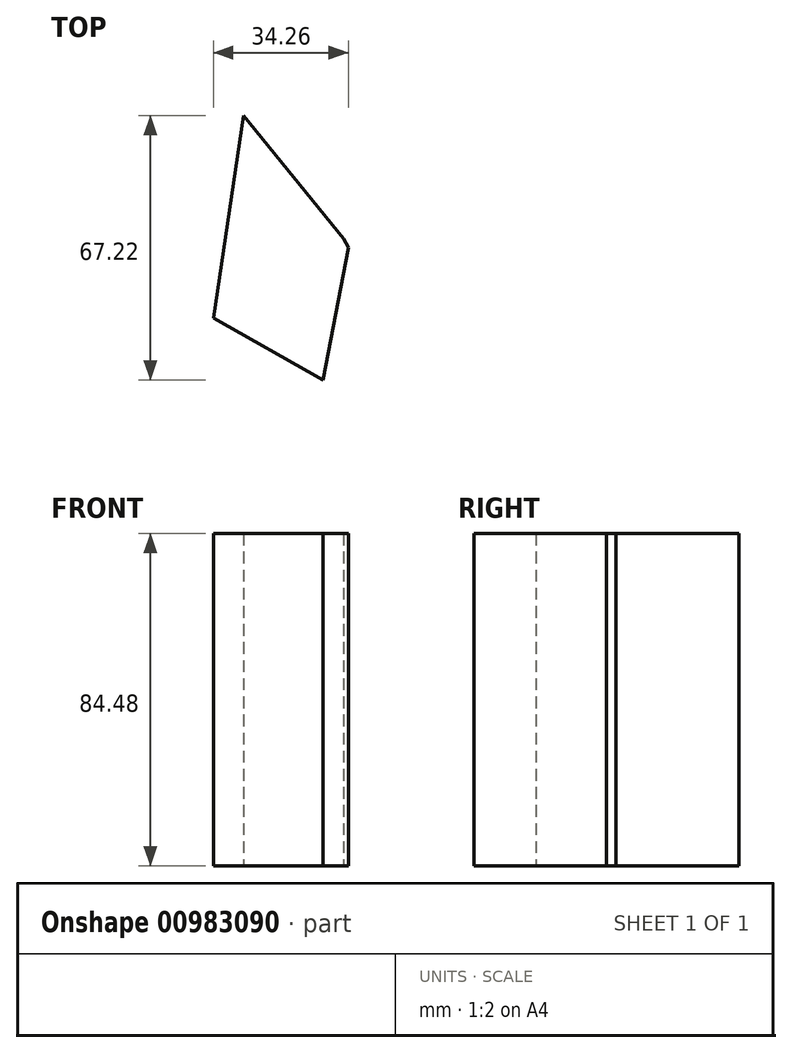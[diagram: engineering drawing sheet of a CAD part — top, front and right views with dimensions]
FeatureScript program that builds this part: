
annotation { "Feature Type Name" : "Feature", "Feature Type Description" : "" }
export const myFeature = defineFeature(function(context is Context, id is Id, definition is map)
    precondition{}
    {
        {
            var Q0;
            Q0=qCreatedBy(makeId("Top.planeOp"),FACE);
            var sketch = newSketch(context, id + "F0", { "sketchPlane" : qUnion([Q0])});
            skLineSegment(sketch, "E0", {"start": v(16.3, -24.25) * mm, "end": v(23.96, 27.28) * mm});
            skLineSegment(sketch, "E1", {"start": v(23.96, 27.28) * mm, "end": v(49.39, -3.98) * mm});
            skLineSegment(sketch, "E2", {"start": v(44.16, -39.94) * mm, "end": v(16.3, -24.25) * mm});
            skLineSegment(sketch, "E3", {"start": v(50.56, -6.33) * mm, "end": v(44.16, -39.94) * mm});
            skLineSegment(sketch, "E4", {"start": v(49.39, -3.98) * mm, "end": v(50.56, -6.33) * mm});
            skSolve(sketch);
        }
        {
            var Q0;
            Q0 = qSketchRegion(id + "F0", true);
            extrude(context, id + "F1", {"entities" : qUnion([Q0]), "depth" : 84.48 * mm, "offsetDistance" : 25.4 * mm});
        }
    });
